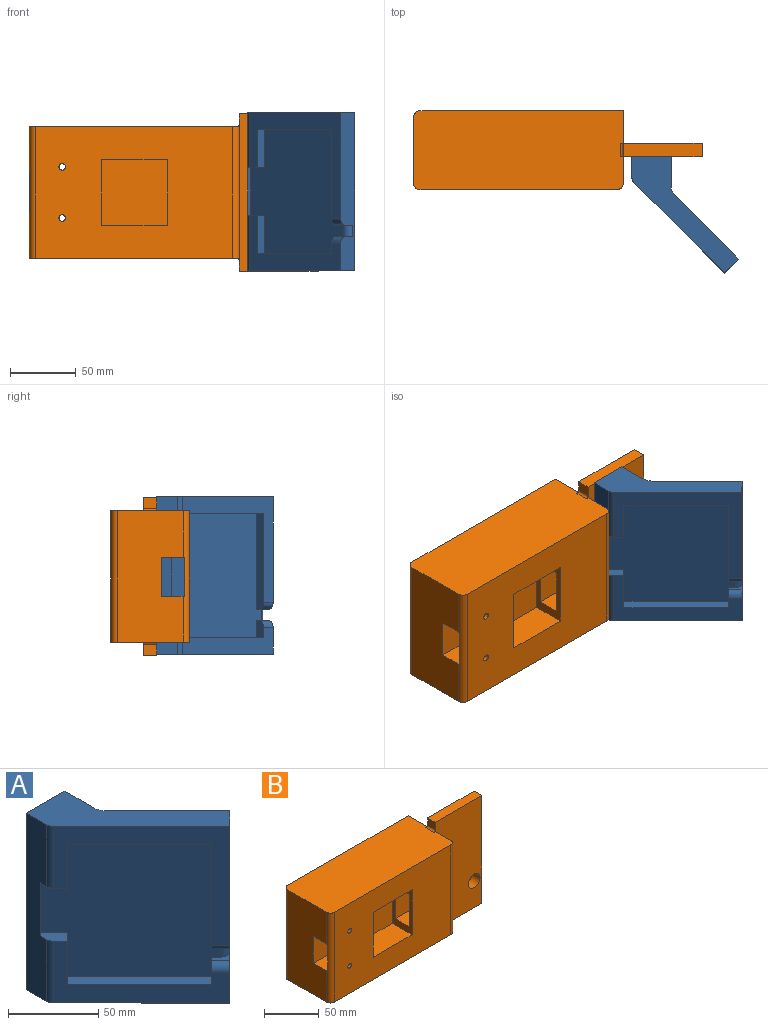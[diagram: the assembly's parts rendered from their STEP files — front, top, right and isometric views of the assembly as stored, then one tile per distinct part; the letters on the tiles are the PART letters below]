
ASSEMBLY  parts=2 mates=1
PART A: 27 faces, bbox 81.3x88.7x120 mm
  f0: plane 69.25x69.25mm, normal (-0.71,-0.71,0), area 1538mm2, adj f3,f4,f10,f13,f14,f18,f21,f24
  f1: plane 29.5x5.66mm, normal (0.71,-0.71,0), area 236mm2, adj f5,f12,f15,f19
  f2: plane 120x15.93mm, normal (-1,0,0), area 1731.5mm2, adj f8,f9,f10,f18,f19,f20,f21,f22
  f3: plane 13x5.66mm, normal (-0.71,0.71,0), area 98.6mm2, adj f0,f14,f15,f17,f24
  f4: plane 120x10.61mm, normal (0.71,-0.71,0), area 1674.9mm2, adj f0,f5,f6,f9,f10,f16,f17,f23
  f5: plane 80.7x69.25mm, normal (-0.71,-0.71,0), area 2140mm2, adj f1,f4,f9,f11,f12,f19,f22,f25
  f6: plane 120x48.39mm, normal (0.71,0.71,0), area 8211.8mm2, adj f4,f9,f10,f26
  f7: plane 120x22.64mm, normal (1,0,0), area 2717.4mm2, adj f8,f9,f10,f26
  f8: plane 120x30mm, normal (0,1,0), area 3600mm2, adj f2,f7,f9,f10
  f9: plane 88.71x81.32mm, normal (0,0,1), area 1967.7mm2, adj f2,f4,f5,f6,f7,f8,f22,f26
  f10: plane 88.71x81.32mm, normal (0,0,-1), area 1967.7mm2, adj f0,f2,f4,f6,f7,f8,f21,f26
  f11: plane 73.2x5.66mm, normal (-0.71,0.71,0), area 580.2mm2, adj f5,f12,f15,f16,f25
  f12: plane 62.23x62.23mm, normal (0,0,-1), area 640mm2, adj f1,f5,f11,f15
  f13: plane 29.5x5.66mm, normal (0.71,-0.71,0), area 236mm2, adj f0,f14,f15,f18
  f14: plane 62.23x62.23mm, normal (0,0,1), area 640mm2, adj f0,f3,f13,f15
  f15: plane 95x70.71mm, normal (-0.71,-0.71,0), area 8184mm2, adj f1,f3,f11,f12,f13,f14,f16,f17
  f16: plane 12.73x9.19mm, normal (0,0,-1), area 35.4mm2, adj f4,f11,f15,f23,f25
  f17: plane 12.73x9.19mm, normal (0,0,1), area 35.4mm2, adj f3,f4,f15,f23,f24
  f18: plane 16.26x12.73mm, normal (0,0,1), area 107mm2, adj f0,f2,f13,f15,f20,f21
  f19: plane 16.26x12.73mm, normal (0,0,-1), area 107mm2, adj f1,f2,f5,f15,f20,f22
  f20: plane 36x2.12mm, normal (0.71,-0.71,0), area 108mm2, adj f2,f15,f18,f19
  f21: cylinder r=5mm len=42mm, axis (0,0,1), area 164.9mm2, adj f0,f2,f10,f18
  f22: cylinder r=5mm len=42mm, axis (0,0,1), area 164.9mm2, adj f2,f5,f9,f19
  f23: cylinder r=5mm len=8.8mm, axis (0,0,-1), area 69.1mm2, adj f4,f15,f16,f17
  f24: cylinder r=5mm len=10.61mm, axis (-0.71,0.71,0), area 78.5mm2, adj f0,f3,f4,f17
  f25: cylinder r=5mm len=10.61mm, axis (0.71,-0.71,0), area 78.5mm2, adj f4,f5,f11,f16
  f26: cylinder r=10mm len=120mm, axis (0,0,1), area 942.5mm2, adj f6,f7,f9,f10
PART B: 40 faces, bbox 220x60x120 mm
  f0: plane 50.1x25.5mm, normal (1,0,0), area 737.5mm2, adj f8,f9,f12,f14,f33,f34,f35,f36
  f1: plane 100x50mm, normal (-1,0,0), area 4497.5mm2, adj f2,f6,f7,f15,f33,f34,f36
  f2: cylinder r=5mm len=100mm, axis (0,0,1), area 747.5mm2, adj f1,f6,f7,f12,f34,f35,f36
  f3: plane 100x20.11mm, normal (1,0,0), area 1407.8mm2, adj f6,f7,f21,f22,f24,f28,f39
  f4: plane 100x24.89mm, normal (1,0,0), area 1769.2mm2, adj f6,f7,f13,f16,f17,f18,f19,f26
  f5: plane 50.1x25.5mm, normal (-1,0,0), area 629.5mm2, adj f8,f9,f12,f14,f21,f22,f23,f24
  f6: plane 160x60mm, normal (0,0,-1), area 9563.9mm2, adj f1,f2,f3,f4,f12,f13,f15,f26
  f7: plane 160x60mm, normal (0,0,1), area 9563.9mm2, adj f1,f2,f3,f4,f12,f13,f15,f26
  f8: plane 50.1x25.5mm, normal (0,0,1), area 1277.5mm2, adj f0,f5,f12,f14
  f9: plane 50.1x25.5mm, normal (0,0,-1), area 1277.5mm2, adj f0,f5,f12,f14
  f10: cylinder r=2.5mm len=60mm, axis (0,1,0), area 942.5mm2, adj f12,f13
  f11: cylinder r=2.5mm len=60mm, axis (0,1,0), area 942.5mm2, adj f12,f13
  f12: plane 150x100mm, normal (0,-1,0), area 12450.7mm2, adj f0,f2,f5,f6,f7,f8,f9,f10
  f13: plane 155x100mm, normal (0,1,0), area 15460.7mm2, adj f4,f6,f7,f10,f11,f15
  f14: plane 50.1x50.1mm, normal (0,-1,0), area 2510mm2, adj f0,f5,f8,f9
  f15: cylinder r=5mm len=100mm, axis (0,0,-1), area 785.4mm2, adj f1,f6,f7,f13
  f16: plane 120x12mm, normal (0,0,1), area 1440mm2, adj f4,f17,f19,f20
  f17: plane 120x60mm, normal (0,-1,0), area 7200mm2, adj f4,f16,f18,f20
  f18: plane 120x12mm, normal (0,0,-1), area 1440mm2, adj f4,f17,f19,f20
  f19: plane 120x60mm, normal (0,1,0), area 7200mm2, adj f4,f16,f18,f20
  f20: plane 60x12mm, normal (1,0,0), area 720mm2, adj f16,f17,f18,f19
  f21: plane 54.95x36mm, normal (0,-1,0), area 1978.2mm2, adj f3,f5,f22,f24
  f22: plane 54.95x18mm, normal (0,0,1), area 989mm2, adj f3,f5,f21,f23,f39
  f23: plane 54.79x36mm, normal (0,1,0), area 1972.5mm2, adj f5,f22,f24,f39
  f24: plane 54.95x18mm, normal (0,0,-1), area 989mm2, adj f3,f5,f21,f23,f39
  f25: plane 10x8mm, normal (-1,0,0), area 80mm2, adj f26,f28,f29,f37
  f26: plane 120x62mm, normal (0,1,0), area 7025mm2, adj f4,f6,f7,f25,f27,f29,f30,f31
  f27: plane 60x10mm, normal (0,0,1), area 600mm2, adj f26,f28,f30,f31
  f28: plane 120x62mm, normal (0,-1,0), area 7025mm2, adj f3,f6,f7,f25,f27,f29,f30,f31
  f29: plane 60x10mm, normal (0,0,-1), area 600mm2, adj f25,f26,f28,f30
  f30: plane 120x10mm, normal (1,0,0), area 1200mm2, adj f26,f27,f28,f29
  f31: plane 10x8mm, normal (-1,0,0), area 80mm2, adj f26,f27,f28,f38
  f32: cylinder r=7.5mm len=15mm, axis (0,-1,0), area 471.2mm2, adj f26,f28
  f33: plane 54.95x30mm, normal (0,-1,0), area 1648.5mm2, adj f0,f1,f34,f36
  f34: plane 54.95x18mm, normal (0,0,-1), area 989mm2, adj f0,f1,f2,f33,f35
  f35: plane 54.79x30mm, normal (0,1,0), area 1643.7mm2, adj f0,f2,f34,f36
  f36: plane 54.95x18mm, normal (0,0,1), area 989mm2, adj f0,f1,f2,f33,f35
  f37: cylinder r=2mm len=10mm, axis (0,1,0), area 31.4mm2, adj f6,f25,f26,f28
  f38: cylinder r=2mm len=10mm, axis (0,-1,0), area 31.4mm2, adj f7,f26,f28,f31
  f39: cylinder r=5mm len=100mm, axis (0,0,-1), area 739.9mm2, adj f3,f6,f7,f12,f22,f23,f24
PLACE A t=(51.79,-86.38,-66.75)mm
PLACE B t=(-70.06,1.87,-7.51)mm
MATE fastened A.f8 <-> B.f28  axis (0,1,0) through (31.43,-33.02,-6.75)mm
